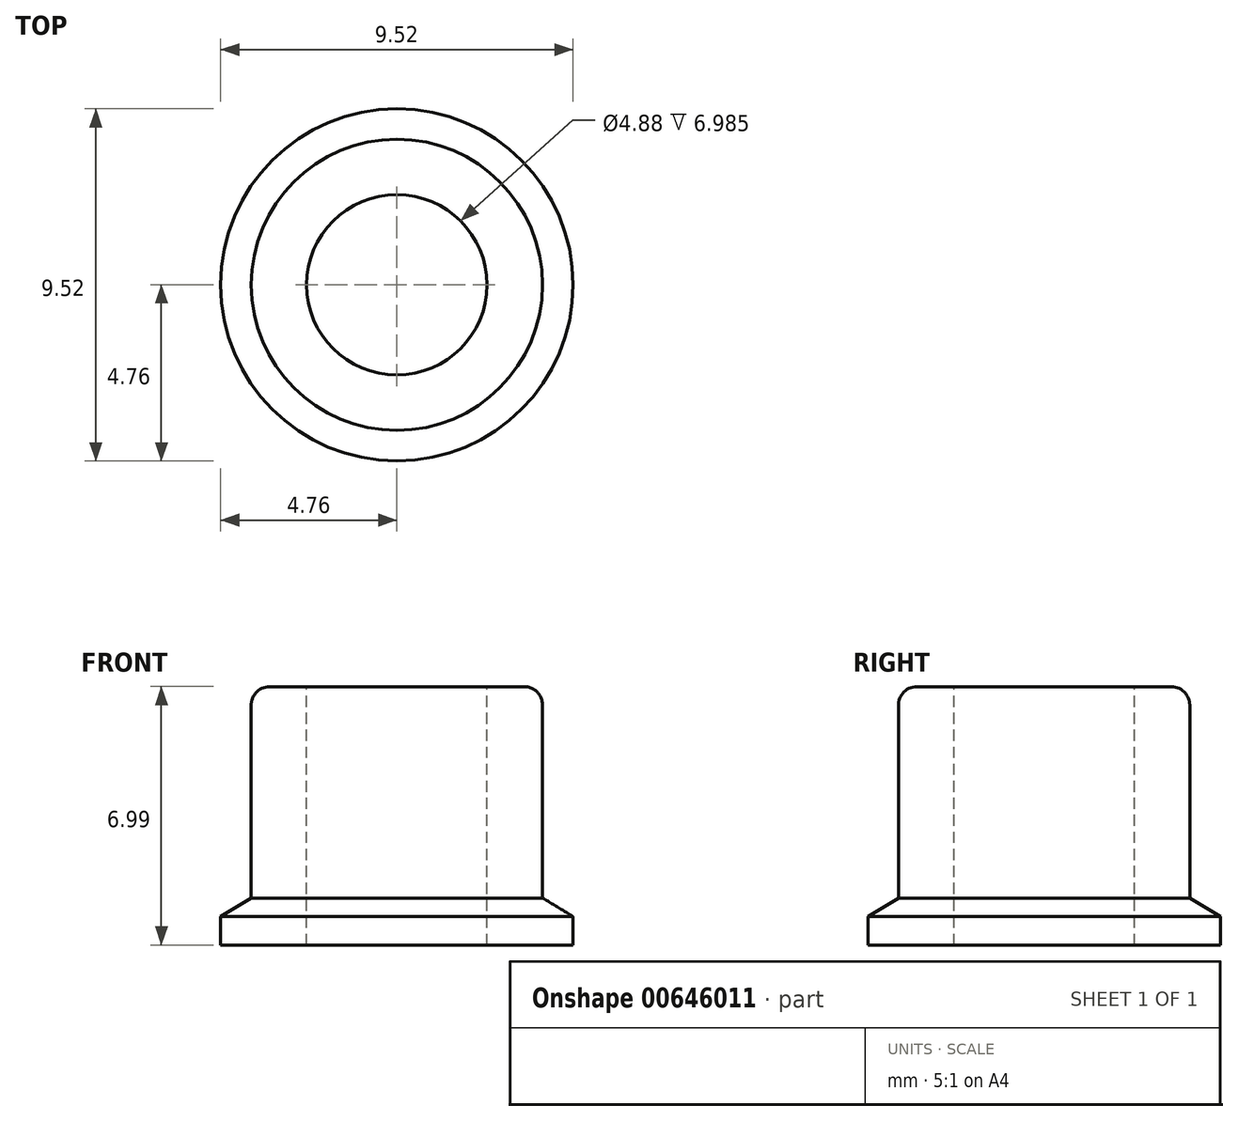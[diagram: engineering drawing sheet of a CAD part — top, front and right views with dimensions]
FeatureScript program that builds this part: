
annotation { "Feature Type Name" : "Feature", "Feature Type Description" : "" }
export const myFeature = defineFeature(function(context is Context, id is Id, definition is map)
    precondition{}
    {
        {
            var Q0;
            Q0=qCreatedBy(makeId("Front.planeOp"),FACE);
            var sketch = newSketch(context, id + "F0", { "sketchPlane" : qUnion([Q0])});
            skLineSegment(sketch, "E0", {"start": v(0, 0) * mm, "end": v(4.76, 0) * mm});
            skLineSegment(sketch, "E1", {"start": v(4.76, 0) * mm, "end": v(4.76, 0.77) * mm});
            skLineSegment(sketch, "E2", {"start": v(4.76, 0.77) * mm, "end": v(3.94, 1.27) * mm});
            skLineSegment(sketch, "E3", {"start": v(3.94, 1.27) * mm, "end": v(3.94, 6.49) * mm});
            skArc(sketch, "E4", {"start": v(3.94, 6.49) * mm, "mid": v(3.8, 6.84) * mm, "end": v(3.44, 6.99) * mm});
            skLineSegment(sketch, "E5", {"start": v(3.44, 6.99) * mm, "end": v(0, 6.99) * mm});
            skLineSegment(sketch, "E6", {"start": v(0, 6.99) * mm, "end": v(0, 0) * mm});
            skSolve(sketch);
        }
        {
            var Q0;
            Q0=makeQuery(id+"F0.imprint","IMPRINT",FACE,{"disambiguationData":[TD([[makeQuery(id+"F0.imprint","IMPRINT",EDGE,{"derivedFrom":sQuery(id+"F0.wireOp",EDGE,"E0")}),1.0]])]});
            var Q1;
            Q1=sQuery(id+"F0.wireOp",EDGE,"E6");
            revolve(context, id + "F1", {"entities" : qUnion([Q0]), "axis" : qUnion([Q1]), "revolveType" : RevolveType.FULL});
        }
        {
            var Q0;
            Q0=makeQuery(id+"F1.opRevolve","SWEPT_FACE",FACE,{"disambiguationData":[OSD([sQuery(id+"F0.wireOp",EDGE,"E5")])]});
            var sketch = newSketch(context, id + "F2", { "sketchPlane" : qUnion([Q0])});
            skCircle(sketch, "E7", {"center": v(0, 0) * mm, "radius": 2.44 * mm});
            skSolve(sketch);
        }
        {
            var Q0;
            Q0 = qSketchRegion(id + "F2", true);
            extrude(context, id + "F3", {"entities" : qUnion([Q0]), "operationType" : NewBodyOperationType.REMOVE, "endBound" : BoundingType.UP_TO_NEXT, "oppositeDirection" : true, "depth" : 25 * mm, "offsetDistance" : 25 * mm});
        }
    });
